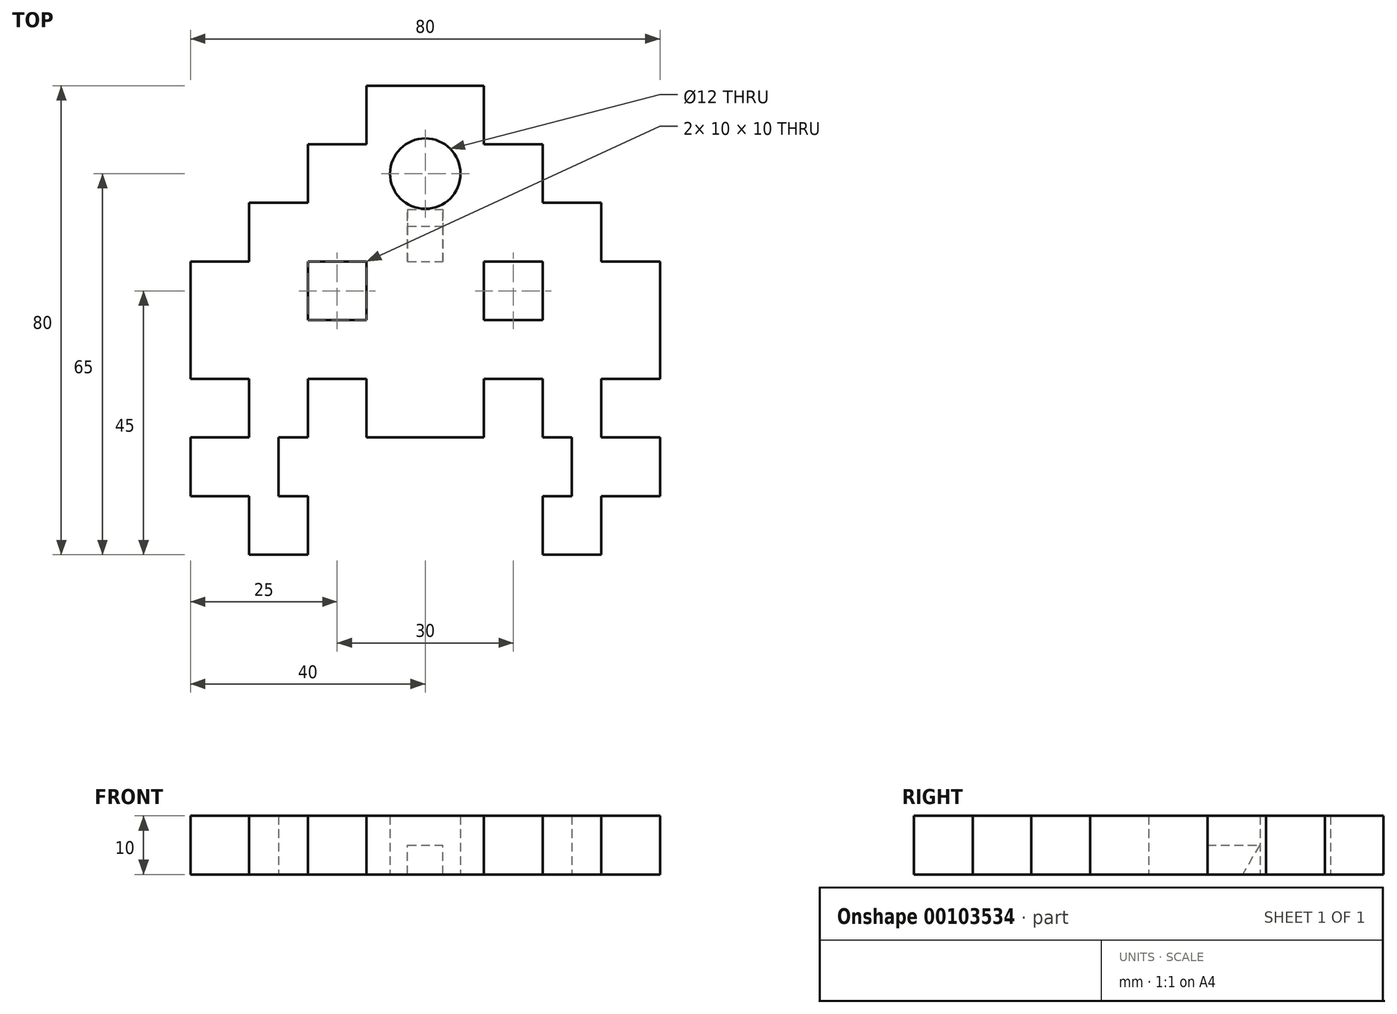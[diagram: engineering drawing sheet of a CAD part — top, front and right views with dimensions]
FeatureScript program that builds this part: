
annotation { "Feature Type Name" : "Feature", "Feature Type Description" : "" }
export const myFeature = defineFeature(function(context is Context, id is Id, definition is map)
    precondition{}
    {
        {
            var Q0;
            Q0=qCreatedBy(makeId("Top.planeOp"),FACE);
            var sketch = newSketch(context, id + "F0", { "sketchPlane" : qUnion([Q0]), "disableImprinting" : false});
            skLineSegment(sketch, "E0", {"start": v(0, 0) * mm, "end": v(-10, 0) * mm});
            skLineSegment(sketch, "E1", {"start": v(-10, 0) * mm, "end": v(-10, -10) * mm});
            skLineSegment(sketch, "E2", {"start": v(-10, -10) * mm, "end": v(-20, -10) * mm});
            skLineSegment(sketch, "E3", {"start": v(-20, -10) * mm, "end": v(-20, -20) * mm});
            skLineSegment(sketch, "E4", {"start": v(-20, -20) * mm, "end": v(-30, -20) * mm});
            skLineSegment(sketch, "E5", {"start": v(-30, -20) * mm, "end": v(-30, -30) * mm});
            skLineSegment(sketch, "E6", {"start": v(-30, -30) * mm, "end": v(-40, -30) * mm});
            skLineSegment(sketch, "E7", {"start": v(-40, -30) * mm, "end": v(-40, -40) * mm});
            skLineSegment(sketch, "E8", {"start": v(-40, -40) * mm, "end": v(-40, -50) * mm});
            skLineSegment(sketch, "E9", {"start": v(-40, -50) * mm, "end": v(-30, -50) * mm});
            skLineSegment(sketch, "E10", {"start": v(-30, -50) * mm, "end": v(-30, -60) * mm});
            skLineSegment(sketch, "E11", {"start": v(-30, -60) * mm, "end": v(-40, -60) * mm});
            skLineSegment(sketch, "E12", {"start": v(-40, -60) * mm, "end": v(-40, -70) * mm});
            skLineSegment(sketch, "E13", {"start": v(-40, -70) * mm, "end": v(-30, -70) * mm});
            skLineSegment(sketch, "E14", {"start": v(-30, -70) * mm, "end": v(-30, -80) * mm});
            skLineSegment(sketch, "E15", {"start": v(-30, -80) * mm, "end": v(-20, -80) * mm});
            skLineSegment(sketch, "E16", {"start": v(-20, -80) * mm, "end": v(-20, -70) * mm});
            skLineSegment(sketch, "E17", {"start": v(-20, -70) * mm, "end": v(-25, -70) * mm});
            skLineSegment(sketch, "E18", {"start": v(-25, -70) * mm, "end": v(-25, -60) * mm});
            skLineSegment(sketch, "E19", {"start": v(-25, -60) * mm, "end": v(-20, -60) * mm});
            skLineSegment(sketch, "E20", {"start": v(-20, -60) * mm, "end": v(-20, -50) * mm});
            skLineSegment(sketch, "E21", {"start": v(-20, -50) * mm, "end": v(-10, -50) * mm});
            skLineSegment(sketch, "E22", {"start": v(-10, -50) * mm, "end": v(-10, -60) * mm});
            skLineSegment(sketch, "E23", {"start": v(-10, -60) * mm, "end": v(0, -60) * mm});
            skLineSegment(sketch, "E24", {"start": v(-30, -70) * mm, "end": v(-25, -70) * mm, "construction": true});
            skLineSegment(sketch, "E25.bottom", {"start": v(-10, -30) * mm, "end": v(-20, -30) * mm});
            skLineSegment(sketch, "E25.top", {"start": v(-10, -40) * mm, "end": v(-20, -40) * mm});
            skLineSegment(sketch, "E25.left", {"start": v(-10, -30) * mm, "end": v(-10, -40) * mm});
            skLineSegment(sketch, "E25.right", {"start": v(-20, -30) * mm, "end": v(-20, -40) * mm});
            skLineSegment(sketch, "E26", {"start": v(0, 0) * mm, "end": v(0, -81.86) * mm, "construction": true});
            skLineSegment(sketch, "E27.MirrorCS", {"start": v(25, -60) * mm, "end": v(20, -60) * mm});
            skLineSegment(sketch, "E28.MirrorCS", {"start": v(20, -70) * mm, "end": v(25, -70) * mm});
            skLineSegment(sketch, "E29.MirrorCS", {"start": v(10, -40) * mm, "end": v(20, -40) * mm});
            skLineSegment(sketch, "E30.MirrorCS", {"start": v(40, -70) * mm, "end": v(30, -70) * mm});
            skLineSegment(sketch, "E31.MirrorCS", {"start": v(30, -70) * mm, "end": v(30, -80) * mm});
            skLineSegment(sketch, "E32.MirrorCS", {"start": v(30, -80) * mm, "end": v(20, -80) * mm});
            skLineSegment(sketch, "E33.MirrorCS", {"start": v(0, 0) * mm, "end": v(10, 0) * mm});
            skLineSegment(sketch, "E34.MirrorCS", {"start": v(10, 0) * mm, "end": v(10, -10) * mm});
            skLineSegment(sketch, "E35.MirrorCS", {"start": v(10, -10) * mm, "end": v(20, -10) * mm});
            skLineSegment(sketch, "E36.MirrorCS", {"start": v(20, -10) * mm, "end": v(20, -20) * mm});
            skLineSegment(sketch, "E37.MirrorCS", {"start": v(20, -20) * mm, "end": v(30, -20) * mm});
            skLineSegment(sketch, "E38.MirrorCS", {"start": v(30, -20) * mm, "end": v(30, -30) * mm});
            skLineSegment(sketch, "E39.MirrorCS", {"start": v(30, -30) * mm, "end": v(40, -30) * mm});
            skLineSegment(sketch, "E40.MirrorCS", {"start": v(40, -30) * mm, "end": v(40, -40) * mm});
            skLineSegment(sketch, "E41.MirrorCS", {"start": v(40, -40) * mm, "end": v(40, -50) * mm});
            skLineSegment(sketch, "E42.MirrorCS", {"start": v(40, -50) * mm, "end": v(30, -50) * mm});
            skLineSegment(sketch, "E43.MirrorCS", {"start": v(30, -50) * mm, "end": v(30, -60) * mm});
            skLineSegment(sketch, "E44.MirrorCS", {"start": v(30, -60) * mm, "end": v(40, -60) * mm});
            skLineSegment(sketch, "E45.MirrorCS", {"start": v(40, -60) * mm, "end": v(40, -70) * mm});
            skLineSegment(sketch, "E46.MirrorCS", {"start": v(10, -30) * mm, "end": v(10, -40) * mm});
            skLineSegment(sketch, "E47.MirrorCS", {"start": v(10, -60) * mm, "end": v(0, -60) * mm});
            skLineSegment(sketch, "E48.MirrorCS", {"start": v(20, -60) * mm, "end": v(20, -50) * mm});
            skLineSegment(sketch, "E49.MirrorCS", {"start": v(25, -70) * mm, "end": v(25, -60) * mm});
            skLineSegment(sketch, "E50.MirrorCS", {"start": v(20, -50) * mm, "end": v(10, -50) * mm});
            skLineSegment(sketch, "E51.MirrorCS", {"start": v(10, -50) * mm, "end": v(10, -60) * mm});
            skLineSegment(sketch, "E52.MirrorCS", {"start": v(10, -30) * mm, "end": v(20, -30) * mm});
            skLineSegment(sketch, "E53.MirrorCS", {"start": v(20, -30) * mm, "end": v(20, -40) * mm});
            skLineSegment(sketch, "E54.MirrorCS", {"start": v(20, -80) * mm, "end": v(20, -70) * mm});
            skCircle(sketch, "E55", {"center": v(0, -15) * mm, "radius": 6 * mm});
            skSolve(sketch);
        }
        {
            var Q0;
            Q0 = qSketchRegion(id + "F0", true);
            extrude(context, id + "F1", {"entities" : qUnion([Q0]), "depth" : 10 * mm});
        }
        {
            var Q0;
            Q0=qCreatedBy(makeId("Right.planeOp"),FACE);
            var sketch = newSketch(context, id + "F2", { "sketchPlane" : qUnion([Q0])});
            skLineSegment(sketch, "E56", {"start": v(-30, 0) * mm, "end": v(-30, 5) * mm});
            skLineSegment(sketch, "E57", {"start": v(-30, 5) * mm, "end": v(-21.11, 5) * mm});
            skLineSegment(sketch, "E58", {"start": v(-21.11, 5) * mm, "end": v(-24, 0) * mm});
            skLineSegment(sketch, "E59", {"start": v(-24, 0) * mm, "end": v(-30, 0) * mm});
            skSolve(sketch);
        }
        {
            var Q0;
            Q0 = qSketchRegion(id + "F2", true);
            extrude(context, id + "F3", {"entities" : qUnion([Q0]), "operationType" : NewBodyOperationType.REMOVE, "oppositeDirection" : true, "depth" : 6 * mm, "symmetric" : true});
        }
    });
